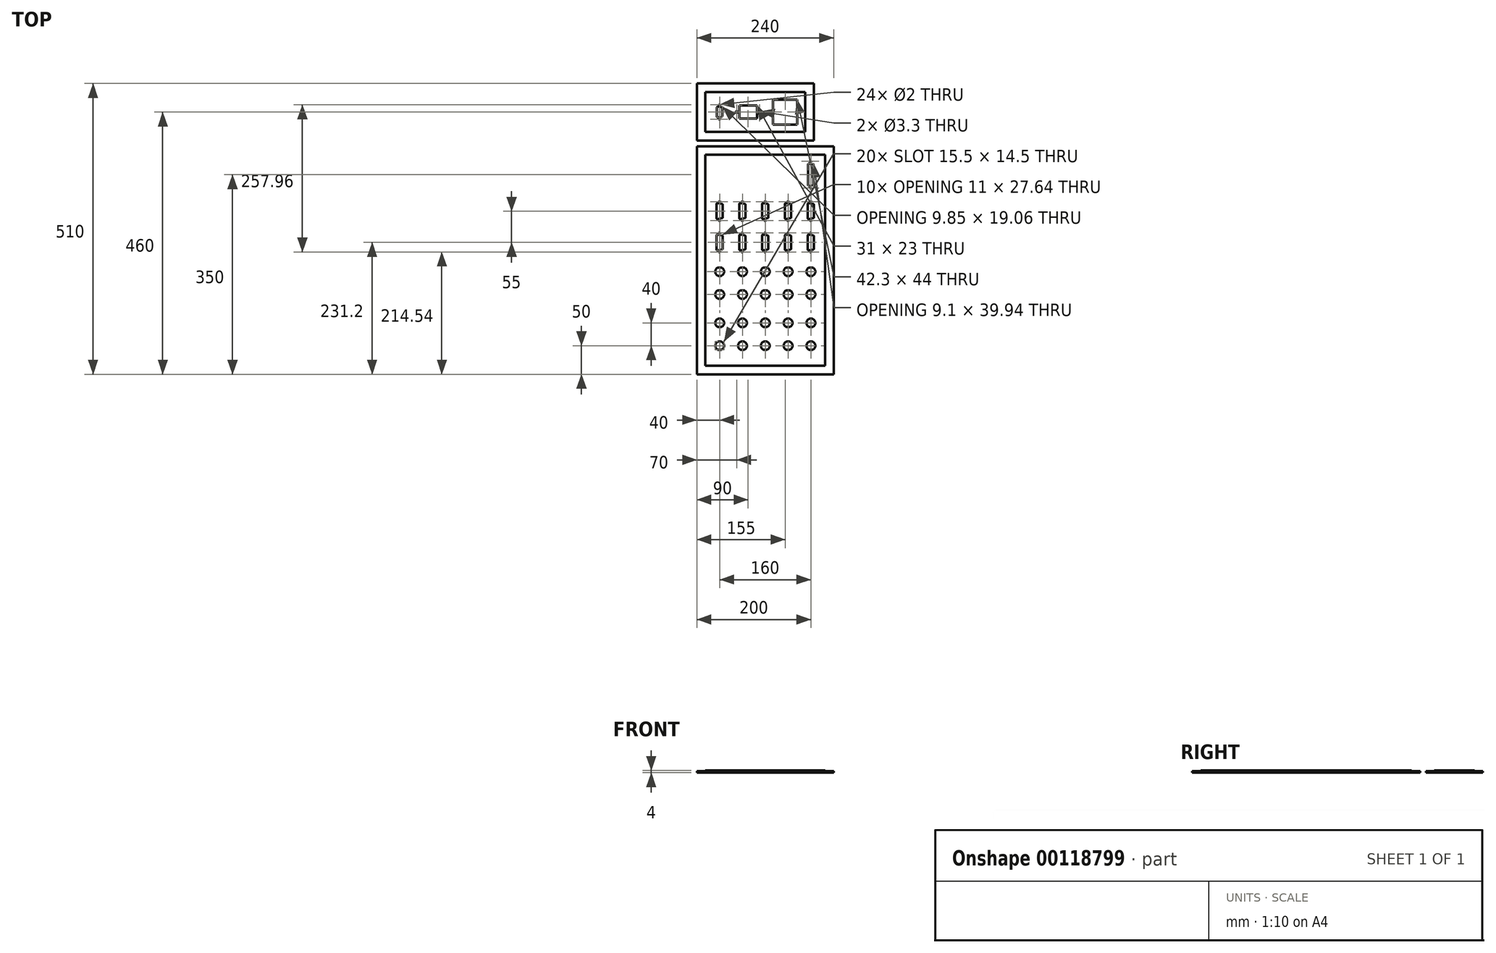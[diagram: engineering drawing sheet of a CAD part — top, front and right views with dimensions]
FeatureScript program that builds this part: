
annotation { "Feature Type Name" : "Feature", "Feature Type Description" : "" }
export const myFeature = defineFeature(function(context is Context, id is Id, definition is map)
    precondition{}
    {
        {
            var Q0;
            Q0=qCreatedBy(makeId("Top.planeOp"),FACE);
            var sketch = newSketch(context, id + "F0", { "sketchPlane" : qUnion([Q0])});
            skLineSegment(sketch, "E0.bottom", {"start": v(-120, -200) * mm, "end": v(120, -200) * mm});
            skLineSegment(sketch, "E0.top", {"start": v(-120, 200) * mm, "end": v(120, 200) * mm});
            skLineSegment(sketch, "E0.left", {"start": v(-120, -200) * mm, "end": v(-120, 200) * mm});
            skLineSegment(sketch, "E0.right", {"start": v(120, -200) * mm, "end": v(120, 200) * mm});
            skArc(sketch, "E1", {"start": v(-82.74, -102.75) * mm, "mid": v(-87.75, -110) * mm, "end": v(-82.74, -117.25) * mm});
            skLineSegment(sketch, "E2", {"start": v(-82.74, -102.75) * mm, "end": v(-77.26, -102.75) * mm});
            skLineSegment(sketch, "E3", {"start": v(-77.26, -117.25) * mm, "end": v(-82.74, -117.25) * mm});
            skLineSegment(sketch, "E4", {"start": v(-80, -110) * mm, "end": v(-87.75, -110) * mm, "construction": true});
            skArc(sketch, "E5.trimOffspring", {"start": v(-77.26, -117.25) * mm, "mid": v(-72.25, -110) * mm, "end": v(-77.26, -102.75) * mm});
            skLineSegment(sketch, "E6.0.1.0", {"start": v(-77.26, -157.25) * mm, "end": v(-82.74, -157.25) * mm});
            skLineSegment(sketch, "E6.0.1.1", {"start": v(-82.74, -142.75) * mm, "end": v(-77.26, -142.75) * mm});
            skArc(sketch, "E6.0.1.2", {"start": v(-82.74, -142.75) * mm, "mid": v(-87.75, -150) * mm, "end": v(-82.74, -157.25) * mm});
            skLineSegment(sketch, "E6.0.1.3", {"start": v(-80, -150) * mm, "end": v(-87.75, -150) * mm, "construction": true});
            skArc(sketch, "E6.0.1.4", {"start": v(-77.26, -157.25) * mm, "mid": v(-72.25, -150) * mm, "end": v(-77.26, -142.75) * mm});
            skLineSegment(sketch, "E6.direction1", {"start": v(-82.74, -117.25) * mm, "end": v(-42.74, -117.25) * mm, "construction": true});
            skLineSegment(sketch, "E6.direction2", {"start": v(-82.74, -117.25) * mm, "end": v(-82.74, -157.25) * mm, "construction": true});
            skLineSegment(sketch, "E7.0.1.0", {"start": v(-37.26, -117.25) * mm, "end": v(-42.74, -117.25) * mm});
            skLineSegment(sketch, "E7.3.1.0", {"start": v(-42.74, -102.75) * mm, "end": v(-37.26, -102.75) * mm});
            skArc(sketch, "E7.6.1.0", {"start": v(-42.74, -102.75) * mm, "mid": v(-47.75, -110) * mm, "end": v(-42.74, -117.25) * mm});
            skLineSegment(sketch, "E7.10.1.0", {"start": v(-40, -110) * mm, "end": v(-47.75, -110) * mm, "construction": true});
            skArc(sketch, "E7.13.1.0", {"start": v(-37.26, -117.25) * mm, "mid": v(-32.25, -110) * mm, "end": v(-37.26, -102.75) * mm});
            skLineSegment(sketch, "E7.0.1.1", {"start": v(-37.26, -157.25) * mm, "end": v(-42.74, -157.25) * mm});
            skLineSegment(sketch, "E7.3.1.1", {"start": v(-42.74, -142.75) * mm, "end": v(-37.26, -142.75) * mm});
            skArc(sketch, "E7.6.1.1", {"start": v(-42.74, -142.75) * mm, "mid": v(-47.75, -150) * mm, "end": v(-42.74, -157.25) * mm});
            skLineSegment(sketch, "E7.10.1.1", {"start": v(-40, -150) * mm, "end": v(-47.75, -150) * mm, "construction": true});
            skArc(sketch, "E7.13.1.1", {"start": v(-37.26, -157.25) * mm, "mid": v(-32.25, -150) * mm, "end": v(-37.26, -142.75) * mm});
            skLineSegment(sketch, "E7.0.2.0", {"start": v(2.74, -117.25) * mm, "end": v(-2.74, -117.25) * mm});
            skLineSegment(sketch, "E7.3.2.0", {"start": v(-2.74, -102.75) * mm, "end": v(2.74, -102.75) * mm});
            skArc(sketch, "E7.6.2.0", {"start": v(-2.74, -102.75) * mm, "mid": v(-7.75, -110) * mm, "end": v(-2.74, -117.25) * mm});
            skLineSegment(sketch, "E7.10.2.0", {"start": v(0, -110) * mm, "end": v(-7.75, -110) * mm, "construction": true});
            skArc(sketch, "E7.13.2.0", {"start": v(2.74, -117.25) * mm, "mid": v(7.75, -110) * mm, "end": v(2.74, -102.75) * mm});
            skLineSegment(sketch, "E7.0.2.1", {"start": v(2.74, -157.25) * mm, "end": v(-2.74, -157.25) * mm});
            skLineSegment(sketch, "E7.3.2.1", {"start": v(-2.74, -142.75) * mm, "end": v(2.74, -142.75) * mm});
            skArc(sketch, "E7.6.2.1", {"start": v(-2.74, -142.75) * mm, "mid": v(-7.75, -150) * mm, "end": v(-2.74, -157.25) * mm});
            skLineSegment(sketch, "E7.10.2.1", {"start": v(0, -150) * mm, "end": v(-7.75, -150) * mm, "construction": true});
            skArc(sketch, "E7.13.2.1", {"start": v(2.74, -157.25) * mm, "mid": v(7.75, -150) * mm, "end": v(2.74, -142.75) * mm});
            skLineSegment(sketch, "E7.0.3.0", {"start": v(42.74, -117.25) * mm, "end": v(37.26, -117.25) * mm});
            skLineSegment(sketch, "E7.3.3.0", {"start": v(37.26, -102.75) * mm, "end": v(42.74, -102.75) * mm});
            skArc(sketch, "E7.6.3.0", {"start": v(37.26, -102.75) * mm, "mid": v(32.25, -110) * mm, "end": v(37.26, -117.25) * mm});
            skLineSegment(sketch, "E7.10.3.0", {"start": v(40, -110) * mm, "end": v(32.25, -110) * mm, "construction": true});
            skArc(sketch, "E7.13.3.0", {"start": v(42.74, -117.25) * mm, "mid": v(47.75, -110) * mm, "end": v(42.74, -102.75) * mm});
            skLineSegment(sketch, "E7.0.3.1", {"start": v(42.74, -157.25) * mm, "end": v(37.26, -157.25) * mm});
            skLineSegment(sketch, "E7.3.3.1", {"start": v(37.26, -142.75) * mm, "end": v(42.74, -142.75) * mm});
            skArc(sketch, "E7.6.3.1", {"start": v(37.26, -142.75) * mm, "mid": v(32.25, -150) * mm, "end": v(37.26, -157.25) * mm});
            skLineSegment(sketch, "E7.10.3.1", {"start": v(40, -150) * mm, "end": v(32.25, -150) * mm, "construction": true});
            skArc(sketch, "E7.13.3.1", {"start": v(42.74, -157.25) * mm, "mid": v(47.75, -150) * mm, "end": v(42.74, -142.75) * mm});
            skLineSegment(sketch, "E7.0.4.0", {"start": v(82.74, -117.25) * mm, "end": v(77.26, -117.25) * mm});
            skLineSegment(sketch, "E7.3.4.0", {"start": v(77.26, -102.75) * mm, "end": v(82.74, -102.75) * mm});
            skArc(sketch, "E7.6.4.0", {"start": v(77.26, -102.75) * mm, "mid": v(72.25, -110) * mm, "end": v(77.26, -117.25) * mm});
            skLineSegment(sketch, "E7.10.4.0", {"start": v(80, -110) * mm, "end": v(72.25, -110) * mm, "construction": true});
            skArc(sketch, "E7.13.4.0", {"start": v(82.74, -117.25) * mm, "mid": v(87.75, -110) * mm, "end": v(82.74, -102.75) * mm});
            skLineSegment(sketch, "E7.0.4.1", {"start": v(82.74, -157.25) * mm, "end": v(77.26, -157.25) * mm});
            skLineSegment(sketch, "E7.3.4.1", {"start": v(77.26, -142.75) * mm, "end": v(82.74, -142.75) * mm});
            skArc(sketch, "E7.6.4.1", {"start": v(77.26, -142.75) * mm, "mid": v(72.25, -150) * mm, "end": v(77.26, -157.25) * mm});
            skLineSegment(sketch, "E7.10.4.1", {"start": v(80, -150) * mm, "end": v(72.25, -150) * mm, "construction": true});
            skArc(sketch, "E7.13.4.1", {"start": v(82.74, -157.25) * mm, "mid": v(87.75, -150) * mm, "end": v(82.74, -142.75) * mm});
            skLineSegment(sketch, "E8.bottom", {"start": v(-105, 185) * mm, "end": v(105, 185) * mm, "construction": true});
            skLineSegment(sketch, "E8.top", {"start": v(-105, -185) * mm, "end": v(105, -185) * mm, "construction": true});
            skLineSegment(sketch, "E8.left", {"start": v(-105, 185) * mm, "end": v(-105, -185) * mm, "construction": true});
            skLineSegment(sketch, "E8.right", {"start": v(105, 185) * mm, "end": v(105, -185) * mm, "construction": true});
            skArc(sketch, "E9", {"start": v(-82.74, -12.75) * mm, "mid": v(-87.75, -20) * mm, "end": v(-82.74, -27.25) * mm});
            skLineSegment(sketch, "E10", {"start": v(-82.74, -12.75) * mm, "end": v(-77.26, -12.75) * mm});
            skLineSegment(sketch, "E11", {"start": v(-77.26, -27.25) * mm, "end": v(-82.74, -27.25) * mm});
            skLineSegment(sketch, "E12", {"start": v(-80, -20) * mm, "end": v(-87.75, -20) * mm, "construction": true});
            skArc(sketch, "E13.trimOffspring", {"start": v(-77.26, -27.25) * mm, "mid": v(-72.25, -20) * mm, "end": v(-77.26, -12.75) * mm});
            skLineSegment(sketch, "E14", {"start": v(-83.74, 100) * mm, "end": v(-75.74, 98.59) * mm});
            skLineSegment(sketch, "E15", {"start": v(-74.5, 97.11) * mm, "end": v(-74.5, 75.29) * mm});
            skLineSegment(sketch, "E16", {"start": v(-75.74, 73.81) * mm, "end": v(-83.74, 72.4) * mm});
            skLineSegment(sketch, "E17", {"start": v(-85.5, 73.88) * mm, "end": v(-85.5, 98.52) * mm});
            skLineSegment(sketch, "E18", {"start": v(-80, 99.34) * mm, "end": v(-80, 73.06) * mm, "construction": true});
            skPoint(sketch, "E19.visualSharp", {"position": v(-85.5, 100.31) * mm});
            skArc(sketch, "E19.filletArc", {"start": v(-83.74, 100) * mm, "mid": v(-84.96, 99.67) * mm, "end": v(-85.5, 98.52) * mm});
            skPoint(sketch, "E20.visualSharp", {"position": v(-74.5, 98.37) * mm});
            skArc(sketch, "E20.filletArc", {"start": v(-74.5, 97.11) * mm, "mid": v(-74.85, 98.08) * mm, "end": v(-75.74, 98.59) * mm});
            skPoint(sketch, "E21.visualSharp", {"position": v(-74.5, 74.03) * mm});
            skArc(sketch, "E21.filletArc", {"start": v(-75.74, 73.81) * mm, "mid": v(-74.85, 74.32) * mm, "end": v(-74.5, 75.29) * mm});
            skPoint(sketch, "E22.visualSharp", {"position": v(-85.5, 72.09) * mm});
            skArc(sketch, "E22.filletArc", {"start": v(-85.5, 73.88) * mm, "mid": v(-84.96, 72.73) * mm, "end": v(-83.74, 72.4) * mm});
            skCircle(sketch, "E23", {"center": v(-80, 102.86) * mm, "radius": 1 * mm});
            skCircle(sketch, "E24", {"center": v(-80, 69.54) * mm, "radius": 1 * mm});
            skLineSegment(sketch, "E25", {"start": v(-84, 86.2) * mm, "end": v(-76.01, 86.2) * mm, "construction": true});
            skPoint(sketch, "E26.0.1.0", {"position": v(-85.5, 45.31) * mm});
            skPoint(sketch, "E26.0.1.1", {"position": v(-85.5, 17.09) * mm});
            skPoint(sketch, "E26.0.1.2", {"position": v(-74.5, 43.37) * mm});
            skLineSegment(sketch, "E26.0.1.3", {"start": v(-80, 44.34) * mm, "end": v(-80, 18.06) * mm, "construction": true});
            skLineSegment(sketch, "E26.0.1.4", {"start": v(-84, 31.2) * mm, "end": v(-76.01, 31.2) * mm, "construction": true});
            skPoint(sketch, "E26.0.1.5", {"position": v(-74.5, 19.03) * mm});
            skLineSegment(sketch, "E26.0.1.6", {"start": v(-74.5, 42.11) * mm, "end": v(-74.5, 20.29) * mm});
            skLineSegment(sketch, "E26.0.1.7", {"start": v(-85.5, 18.88) * mm, "end": v(-85.5, 43.52) * mm});
            skCircle(sketch, "E26.0.1.8", {"center": v(-80, 47.86) * mm, "radius": 1 * mm});
            skLineSegment(sketch, "E26.0.1.9", {"start": v(-83.74, 45) * mm, "end": v(-75.74, 43.59) * mm});
            skCircle(sketch, "E26.0.1.10", {"center": v(-80, 14.54) * mm, "radius": 1 * mm});
            skArc(sketch, "E26.0.1.11", {"start": v(-83.74, 45) * mm, "mid": v(-84.96, 44.67) * mm, "end": v(-85.5, 43.52) * mm});
            skArc(sketch, "E26.0.1.12", {"start": v(-85.5, 18.88) * mm, "mid": v(-84.96, 17.73) * mm, "end": v(-83.74, 17.4) * mm});
            skLineSegment(sketch, "E26.0.1.13", {"start": v(-75.74, 18.81) * mm, "end": v(-83.74, 17.4) * mm});
            skArc(sketch, "E26.0.1.14", {"start": v(-75.74, 18.81) * mm, "mid": v(-74.85, 19.32) * mm, "end": v(-74.5, 20.29) * mm});
            skArc(sketch, "E26.0.1.15", {"start": v(-74.5, 42.11) * mm, "mid": v(-74.85, 43.08) * mm, "end": v(-75.74, 43.59) * mm});
            skPoint(sketch, "E26.1.0.0", {"position": v(-45.5, 100.31) * mm});
            skPoint(sketch, "E26.1.0.1", {"position": v(-45.5, 72.09) * mm});
            skPoint(sketch, "E26.1.0.2", {"position": v(-34.5, 98.37) * mm});
            skLineSegment(sketch, "E26.1.0.3", {"start": v(-40, 99.34) * mm, "end": v(-40, 73.06) * mm, "construction": true});
            skLineSegment(sketch, "E26.1.0.4", {"start": v(-44, 86.2) * mm, "end": v(-36.01, 86.2) * mm, "construction": true});
            skPoint(sketch, "E26.1.0.5", {"position": v(-34.5, 74.03) * mm});
            skLineSegment(sketch, "E26.1.0.6", {"start": v(-34.5, 97.11) * mm, "end": v(-34.5, 75.29) * mm});
            skLineSegment(sketch, "E26.1.0.7", {"start": v(-45.5, 73.88) * mm, "end": v(-45.5, 98.52) * mm});
            skCircle(sketch, "E26.1.0.8", {"center": v(-40, 102.86) * mm, "radius": 1 * mm});
            skLineSegment(sketch, "E26.1.0.9", {"start": v(-43.74, 100) * mm, "end": v(-35.74, 98.59) * mm});
            skCircle(sketch, "E26.1.0.10", {"center": v(-40, 69.54) * mm, "radius": 1 * mm});
            skArc(sketch, "E26.1.0.11", {"start": v(-43.74, 100) * mm, "mid": v(-44.96, 99.67) * mm, "end": v(-45.5, 98.52) * mm});
            skArc(sketch, "E26.1.0.12", {"start": v(-45.5, 73.88) * mm, "mid": v(-44.96, 72.73) * mm, "end": v(-43.74, 72.4) * mm});
            skLineSegment(sketch, "E26.1.0.13", {"start": v(-35.74, 73.81) * mm, "end": v(-43.74, 72.4) * mm});
            skArc(sketch, "E26.1.0.14", {"start": v(-35.74, 73.81) * mm, "mid": v(-34.85, 74.32) * mm, "end": v(-34.5, 75.29) * mm});
            skArc(sketch, "E26.1.0.15", {"start": v(-34.5, 97.11) * mm, "mid": v(-34.85, 98.08) * mm, "end": v(-35.74, 98.59) * mm});
            skPoint(sketch, "E26.1.1.0", {"position": v(-45.5, 45.31) * mm});
            skPoint(sketch, "E26.1.1.1", {"position": v(-45.5, 17.09) * mm});
            skPoint(sketch, "E26.1.1.2", {"position": v(-34.5, 43.37) * mm});
            skLineSegment(sketch, "E26.1.1.3", {"start": v(-40, 44.34) * mm, "end": v(-40, 18.06) * mm, "construction": true});
            skLineSegment(sketch, "E26.1.1.4", {"start": v(-44, 31.2) * mm, "end": v(-36.01, 31.2) * mm, "construction": true});
            skPoint(sketch, "E26.1.1.5", {"position": v(-34.5, 19.03) * mm});
            skLineSegment(sketch, "E26.1.1.6", {"start": v(-34.5, 42.11) * mm, "end": v(-34.5, 20.29) * mm});
            skLineSegment(sketch, "E26.1.1.7", {"start": v(-45.5, 18.88) * mm, "end": v(-45.5, 43.52) * mm});
            skCircle(sketch, "E26.1.1.8", {"center": v(-40, 47.86) * mm, "radius": 1 * mm});
            skLineSegment(sketch, "E26.1.1.9", {"start": v(-43.74, 45) * mm, "end": v(-35.74, 43.59) * mm});
            skCircle(sketch, "E26.1.1.10", {"center": v(-40, 14.54) * mm, "radius": 1 * mm});
            skArc(sketch, "E26.1.1.11", {"start": v(-43.74, 45) * mm, "mid": v(-44.96, 44.67) * mm, "end": v(-45.5, 43.52) * mm});
            skArc(sketch, "E26.1.1.12", {"start": v(-45.5, 18.88) * mm, "mid": v(-44.96, 17.73) * mm, "end": v(-43.74, 17.4) * mm});
            skLineSegment(sketch, "E26.1.1.13", {"start": v(-35.74, 18.81) * mm, "end": v(-43.74, 17.4) * mm});
            skArc(sketch, "E26.1.1.14", {"start": v(-35.74, 18.81) * mm, "mid": v(-34.85, 19.32) * mm, "end": v(-34.5, 20.29) * mm});
            skArc(sketch, "E26.1.1.15", {"start": v(-34.5, 42.11) * mm, "mid": v(-34.85, 43.08) * mm, "end": v(-35.74, 43.59) * mm});
            skPoint(sketch, "E26.2.0.0", {"position": v(-5.5, 100.31) * mm});
            skPoint(sketch, "E26.2.0.1", {"position": v(-5.5, 72.09) * mm});
            skPoint(sketch, "E26.2.0.2", {"position": v(5.5, 98.37) * mm});
            skLineSegment(sketch, "E26.2.0.3", {"start": v(0, 99.34) * mm, "end": v(0, 73.06) * mm, "construction": true});
            skLineSegment(sketch, "E26.2.0.4", {"start": v(-4, 86.2) * mm, "end": v(3.99, 86.2) * mm, "construction": true});
            skPoint(sketch, "E26.2.0.5", {"position": v(5.5, 74.03) * mm});
            skLineSegment(sketch, "E26.2.0.6", {"start": v(5.5, 97.11) * mm, "end": v(5.5, 75.29) * mm});
            skLineSegment(sketch, "E26.2.0.7", {"start": v(-5.5, 73.88) * mm, "end": v(-5.5, 98.52) * mm});
            skCircle(sketch, "E26.2.0.8", {"center": v(0, 102.86) * mm, "radius": 1 * mm});
            skLineSegment(sketch, "E26.2.0.9", {"start": v(-3.74, 100) * mm, "end": v(4.26, 98.59) * mm});
            skCircle(sketch, "E26.2.0.10", {"center": v(0, 69.54) * mm, "radius": 1 * mm});
            skArc(sketch, "E26.2.0.11", {"start": v(-3.74, 100) * mm, "mid": v(-4.96, 99.67) * mm, "end": v(-5.5, 98.52) * mm});
            skArc(sketch, "E26.2.0.12", {"start": v(-5.5, 73.88) * mm, "mid": v(-4.96, 72.73) * mm, "end": v(-3.74, 72.4) * mm});
            skLineSegment(sketch, "E26.2.0.13", {"start": v(4.26, 73.81) * mm, "end": v(-3.74, 72.4) * mm});
            skArc(sketch, "E26.2.0.14", {"start": v(4.26, 73.81) * mm, "mid": v(5.15, 74.32) * mm, "end": v(5.5, 75.29) * mm});
            skArc(sketch, "E26.2.0.15", {"start": v(5.5, 97.11) * mm, "mid": v(5.15, 98.08) * mm, "end": v(4.26, 98.59) * mm});
            skPoint(sketch, "E26.2.1.0", {"position": v(-5.5, 45.31) * mm});
            skPoint(sketch, "E26.2.1.1", {"position": v(-5.5, 17.09) * mm});
            skPoint(sketch, "E26.2.1.2", {"position": v(5.5, 43.37) * mm});
            skLineSegment(sketch, "E26.2.1.3", {"start": v(0, 44.34) * mm, "end": v(0, 18.06) * mm, "construction": true});
            skLineSegment(sketch, "E26.2.1.4", {"start": v(-4, 31.2) * mm, "end": v(3.99, 31.2) * mm, "construction": true});
            skPoint(sketch, "E26.2.1.5", {"position": v(5.5, 19.03) * mm});
            skLineSegment(sketch, "E26.2.1.6", {"start": v(5.5, 42.11) * mm, "end": v(5.5, 20.29) * mm});
            skLineSegment(sketch, "E26.2.1.7", {"start": v(-5.5, 18.88) * mm, "end": v(-5.5, 43.52) * mm});
            skCircle(sketch, "E26.2.1.8", {"center": v(0, 47.86) * mm, "radius": 1 * mm});
            skLineSegment(sketch, "E26.2.1.9", {"start": v(-3.74, 45) * mm, "end": v(4.26, 43.59) * mm});
            skCircle(sketch, "E26.2.1.10", {"center": v(0, 14.54) * mm, "radius": 1 * mm});
            skArc(sketch, "E26.2.1.11", {"start": v(-3.74, 45) * mm, "mid": v(-4.96, 44.67) * mm, "end": v(-5.5, 43.52) * mm});
            skArc(sketch, "E26.2.1.12", {"start": v(-5.5, 18.88) * mm, "mid": v(-4.96, 17.73) * mm, "end": v(-3.74, 17.4) * mm});
            skLineSegment(sketch, "E26.2.1.13", {"start": v(4.26, 18.81) * mm, "end": v(-3.74, 17.4) * mm});
            skArc(sketch, "E26.2.1.14", {"start": v(4.26, 18.81) * mm, "mid": v(5.15, 19.32) * mm, "end": v(5.5, 20.29) * mm});
            skArc(sketch, "E26.2.1.15", {"start": v(5.5, 42.11) * mm, "mid": v(5.15, 43.08) * mm, "end": v(4.26, 43.59) * mm});
            skPoint(sketch, "E26.3.0.0", {"position": v(34.5, 100.31) * mm});
            skPoint(sketch, "E26.3.0.1", {"position": v(34.5, 72.09) * mm});
            skPoint(sketch, "E26.3.0.2", {"position": v(45.5, 98.37) * mm});
            skLineSegment(sketch, "E26.3.0.3", {"start": v(40, 99.34) * mm, "end": v(40, 73.06) * mm, "construction": true});
            skLineSegment(sketch, "E26.3.0.4", {"start": v(36, 86.2) * mm, "end": v(43.99, 86.2) * mm, "construction": true});
            skPoint(sketch, "E26.3.0.5", {"position": v(45.5, 74.03) * mm});
            skLineSegment(sketch, "E26.3.0.6", {"start": v(45.5, 97.11) * mm, "end": v(45.5, 75.29) * mm});
            skLineSegment(sketch, "E26.3.0.7", {"start": v(34.5, 73.88) * mm, "end": v(34.5, 98.52) * mm});
            skCircle(sketch, "E26.3.0.8", {"center": v(40, 102.86) * mm, "radius": 1 * mm});
            skLineSegment(sketch, "E26.3.0.9", {"start": v(36.26, 100) * mm, "end": v(44.26, 98.59) * mm});
            skCircle(sketch, "E26.3.0.10", {"center": v(40, 69.54) * mm, "radius": 1 * mm});
            skArc(sketch, "E26.3.0.11", {"start": v(36.26, 100) * mm, "mid": v(35.04, 99.67) * mm, "end": v(34.5, 98.52) * mm});
            skArc(sketch, "E26.3.0.12", {"start": v(34.5, 73.88) * mm, "mid": v(35.04, 72.73) * mm, "end": v(36.26, 72.4) * mm});
            skLineSegment(sketch, "E26.3.0.13", {"start": v(44.26, 73.81) * mm, "end": v(36.26, 72.4) * mm});
            skArc(sketch, "E26.3.0.14", {"start": v(44.26, 73.81) * mm, "mid": v(45.15, 74.32) * mm, "end": v(45.5, 75.29) * mm});
            skArc(sketch, "E26.3.0.15", {"start": v(45.5, 97.11) * mm, "mid": v(45.15, 98.08) * mm, "end": v(44.26, 98.59) * mm});
            skPoint(sketch, "E26.3.1.0", {"position": v(34.5, 45.31) * mm});
            skPoint(sketch, "E26.3.1.1", {"position": v(34.5, 17.09) * mm});
            skPoint(sketch, "E26.3.1.2", {"position": v(45.5, 43.37) * mm});
            skLineSegment(sketch, "E26.3.1.3", {"start": v(40, 44.34) * mm, "end": v(40, 18.06) * mm, "construction": true});
            skLineSegment(sketch, "E26.3.1.4", {"start": v(36, 31.2) * mm, "end": v(43.99, 31.2) * mm, "construction": true});
            skPoint(sketch, "E26.3.1.5", {"position": v(45.5, 19.03) * mm});
            skLineSegment(sketch, "E26.3.1.6", {"start": v(45.5, 42.11) * mm, "end": v(45.5, 20.29) * mm});
            skLineSegment(sketch, "E26.3.1.7", {"start": v(34.5, 18.88) * mm, "end": v(34.5, 43.52) * mm});
            skCircle(sketch, "E26.3.1.8", {"center": v(40, 47.86) * mm, "radius": 1 * mm});
            skLineSegment(sketch, "E26.3.1.9", {"start": v(36.26, 45) * mm, "end": v(44.26, 43.59) * mm});
            skCircle(sketch, "E26.3.1.10", {"center": v(40, 14.54) * mm, "radius": 1 * mm});
            skArc(sketch, "E26.3.1.11", {"start": v(36.26, 45) * mm, "mid": v(35.04, 44.67) * mm, "end": v(34.5, 43.52) * mm});
            skArc(sketch, "E26.3.1.12", {"start": v(34.5, 18.88) * mm, "mid": v(35.04, 17.73) * mm, "end": v(36.26, 17.4) * mm});
            skLineSegment(sketch, "E26.3.1.13", {"start": v(44.26, 18.81) * mm, "end": v(36.26, 17.4) * mm});
            skArc(sketch, "E26.3.1.14", {"start": v(44.26, 18.81) * mm, "mid": v(45.15, 19.32) * mm, "end": v(45.5, 20.29) * mm});
            skArc(sketch, "E26.3.1.15", {"start": v(45.5, 42.11) * mm, "mid": v(45.15, 43.08) * mm, "end": v(44.26, 43.59) * mm});
            skPoint(sketch, "E26.4.0.0", {"position": v(74.5, 100.31) * mm});
            skPoint(sketch, "E26.4.0.1", {"position": v(74.5, 72.09) * mm});
            skPoint(sketch, "E26.4.0.2", {"position": v(85.5, 98.37) * mm});
            skLineSegment(sketch, "E26.4.0.3", {"start": v(80, 99.34) * mm, "end": v(80, 73.06) * mm, "construction": true});
            skLineSegment(sketch, "E26.4.0.4", {"start": v(76, 86.2) * mm, "end": v(83.99, 86.2) * mm, "construction": true});
            skPoint(sketch, "E26.4.0.5", {"position": v(85.5, 74.03) * mm});
            skLineSegment(sketch, "E26.4.0.6", {"start": v(85.5, 97.11) * mm, "end": v(85.5, 75.29) * mm});
            skLineSegment(sketch, "E26.4.0.7", {"start": v(74.5, 73.88) * mm, "end": v(74.5, 98.52) * mm});
            skCircle(sketch, "E26.4.0.8", {"center": v(80, 102.86) * mm, "radius": 1 * mm});
            skLineSegment(sketch, "E26.4.0.9", {"start": v(76.26, 100) * mm, "end": v(84.26, 98.59) * mm});
            skCircle(sketch, "E26.4.0.10", {"center": v(80, 69.54) * mm, "radius": 1 * mm});
            skArc(sketch, "E26.4.0.11", {"start": v(76.26, 100) * mm, "mid": v(75.04, 99.67) * mm, "end": v(74.5, 98.52) * mm});
            skArc(sketch, "E26.4.0.12", {"start": v(74.5, 73.88) * mm, "mid": v(75.04, 72.73) * mm, "end": v(76.26, 72.4) * mm});
            skLineSegment(sketch, "E26.4.0.13", {"start": v(84.26, 73.81) * mm, "end": v(76.26, 72.4) * mm});
            skArc(sketch, "E26.4.0.14", {"start": v(84.26, 73.81) * mm, "mid": v(85.15, 74.32) * mm, "end": v(85.5, 75.29) * mm});
            skArc(sketch, "E26.4.0.15", {"start": v(85.5, 97.11) * mm, "mid": v(85.15, 98.08) * mm, "end": v(84.26, 98.59) * mm});
            skPoint(sketch, "E26.4.1.0", {"position": v(74.5, 45.31) * mm});
            skPoint(sketch, "E26.4.1.1", {"position": v(74.5, 17.09) * mm});
            skPoint(sketch, "E26.4.1.2", {"position": v(85.5, 43.37) * mm});
            skLineSegment(sketch, "E26.4.1.3", {"start": v(80, 44.34) * mm, "end": v(80, 18.06) * mm, "construction": true});
            skLineSegment(sketch, "E26.4.1.4", {"start": v(76, 31.2) * mm, "end": v(83.99, 31.2) * mm, "construction": true});
            skPoint(sketch, "E26.4.1.5", {"position": v(85.5, 19.03) * mm});
            skLineSegment(sketch, "E26.4.1.6", {"start": v(85.5, 42.11) * mm, "end": v(85.5, 20.29) * mm});
            skLineSegment(sketch, "E26.4.1.7", {"start": v(74.5, 18.88) * mm, "end": v(74.5, 43.52) * mm});
            skCircle(sketch, "E26.4.1.8", {"center": v(80, 47.86) * mm, "radius": 1 * mm});
            skLineSegment(sketch, "E26.4.1.9", {"start": v(76.26, 45) * mm, "end": v(84.26, 43.59) * mm});
            skCircle(sketch, "E26.4.1.10", {"center": v(80, 14.54) * mm, "radius": 1 * mm});
            skArc(sketch, "E26.4.1.11", {"start": v(76.26, 45) * mm, "mid": v(75.04, 44.67) * mm, "end": v(74.5, 43.52) * mm});
            skArc(sketch, "E26.4.1.12", {"start": v(74.5, 18.88) * mm, "mid": v(75.04, 17.73) * mm, "end": v(76.26, 17.4) * mm});
            skLineSegment(sketch, "E26.4.1.13", {"start": v(84.26, 18.81) * mm, "end": v(76.26, 17.4) * mm});
            skArc(sketch, "E26.4.1.14", {"start": v(84.26, 18.81) * mm, "mid": v(85.15, 19.32) * mm, "end": v(85.5, 20.29) * mm});
            skArc(sketch, "E26.4.1.15", {"start": v(85.5, 42.11) * mm, "mid": v(85.15, 43.08) * mm, "end": v(84.26, 43.59) * mm});
            skLineSegment(sketch, "E26.direction1", {"start": v(-85.5, 72.09) * mm, "end": v(-45.5, 72.09) * mm, "construction": true});
            skLineSegment(sketch, "E26.direction2", {"start": v(-85.5, 72.09) * mm, "end": v(-85.5, 17.09) * mm, "construction": true});
            skLineSegment(sketch, "E27.0.1.0", {"start": v(-80, -60) * mm, "end": v(-87.75, -60) * mm, "construction": true});
            skArc(sketch, "E27.0.1.1", {"start": v(-77.26, -67.25) * mm, "mid": v(-72.25, -60) * mm, "end": v(-77.26, -52.75) * mm});
            skArc(sketch, "E27.0.1.2", {"start": v(-82.74, -52.75) * mm, "mid": v(-87.75, -60) * mm, "end": v(-82.74, -67.25) * mm});
            skLineSegment(sketch, "E27.0.1.3", {"start": v(-82.74, -52.75) * mm, "end": v(-77.26, -52.75) * mm});
            skLineSegment(sketch, "E27.0.1.4", {"start": v(-77.26, -67.25) * mm, "end": v(-82.74, -67.25) * mm});
            skLineSegment(sketch, "E27.1.0.0", {"start": v(-40, -20) * mm, "end": v(-47.75, -20) * mm, "construction": true});
            skArc(sketch, "E27.1.0.1", {"start": v(-37.26, -27.25) * mm, "mid": v(-32.25, -20) * mm, "end": v(-37.26, -12.75) * mm});
            skArc(sketch, "E27.1.0.2", {"start": v(-42.74, -12.75) * mm, "mid": v(-47.75, -20) * mm, "end": v(-42.74, -27.25) * mm});
            skLineSegment(sketch, "E27.1.0.3", {"start": v(-42.74, -12.75) * mm, "end": v(-37.26, -12.75) * mm});
            skLineSegment(sketch, "E27.1.0.4", {"start": v(-37.26, -27.25) * mm, "end": v(-42.74, -27.25) * mm});
            skLineSegment(sketch, "E27.1.1.0", {"start": v(-40, -60) * mm, "end": v(-47.75, -60) * mm, "construction": true});
            skArc(sketch, "E27.1.1.1", {"start": v(-37.26, -67.25) * mm, "mid": v(-32.25, -60) * mm, "end": v(-37.26, -52.75) * mm});
            skArc(sketch, "E27.1.1.2", {"start": v(-42.74, -52.75) * mm, "mid": v(-47.75, -60) * mm, "end": v(-42.74, -67.25) * mm});
            skLineSegment(sketch, "E27.1.1.3", {"start": v(-42.74, -52.75) * mm, "end": v(-37.26, -52.75) * mm});
            skLineSegment(sketch, "E27.1.1.4", {"start": v(-37.26, -67.25) * mm, "end": v(-42.74, -67.25) * mm});
            skLineSegment(sketch, "E27.2.0.0", {"start": v(0, -20) * mm, "end": v(-7.75, -20) * mm, "construction": true});
            skArc(sketch, "E27.2.0.1", {"start": v(2.74, -27.25) * mm, "mid": v(7.75, -20) * mm, "end": v(2.74, -12.75) * mm});
            skArc(sketch, "E27.2.0.2", {"start": v(-2.74, -12.75) * mm, "mid": v(-7.75, -20) * mm, "end": v(-2.74, -27.25) * mm});
            skLineSegment(sketch, "E27.2.0.3", {"start": v(-2.74, -12.75) * mm, "end": v(2.74, -12.75) * mm});
            skLineSegment(sketch, "E27.2.0.4", {"start": v(2.74, -27.25) * mm, "end": v(-2.74, -27.25) * mm});
            skLineSegment(sketch, "E27.2.1.0", {"start": v(0, -60) * mm, "end": v(-7.75, -60) * mm, "construction": true});
            skArc(sketch, "E27.2.1.1", {"start": v(2.74, -67.25) * mm, "mid": v(7.75, -60) * mm, "end": v(2.74, -52.75) * mm});
            skArc(sketch, "E27.2.1.2", {"start": v(-2.74, -52.75) * mm, "mid": v(-7.75, -60) * mm, "end": v(-2.74, -67.25) * mm});
            skLineSegment(sketch, "E27.2.1.3", {"start": v(-2.74, -52.75) * mm, "end": v(2.74, -52.75) * mm});
            skLineSegment(sketch, "E27.2.1.4", {"start": v(2.74, -67.25) * mm, "end": v(-2.74, -67.25) * mm});
            skLineSegment(sketch, "E27.3.0.0", {"start": v(40, -20) * mm, "end": v(32.25, -20) * mm, "construction": true});
            skArc(sketch, "E27.3.0.1", {"start": v(42.74, -27.25) * mm, "mid": v(47.75, -20) * mm, "end": v(42.74, -12.75) * mm});
            skArc(sketch, "E27.3.0.2", {"start": v(37.26, -12.75) * mm, "mid": v(32.25, -20) * mm, "end": v(37.26, -27.25) * mm});
            skLineSegment(sketch, "E27.3.0.3", {"start": v(37.26, -12.75) * mm, "end": v(42.74, -12.75) * mm});
            skLineSegment(sketch, "E27.3.0.4", {"start": v(42.74, -27.25) * mm, "end": v(37.26, -27.25) * mm});
            skLineSegment(sketch, "E27.3.1.0", {"start": v(40, -60) * mm, "end": v(32.25, -60) * mm, "construction": true});
            skArc(sketch, "E27.3.1.1", {"start": v(42.74, -67.25) * mm, "mid": v(47.75, -60) * mm, "end": v(42.74, -52.75) * mm});
            skArc(sketch, "E27.3.1.2", {"start": v(37.26, -52.75) * mm, "mid": v(32.25, -60) * mm, "end": v(37.26, -67.25) * mm});
            skLineSegment(sketch, "E27.3.1.3", {"start": v(37.26, -52.75) * mm, "end": v(42.74, -52.75) * mm});
            skLineSegment(sketch, "E27.3.1.4", {"start": v(42.74, -67.25) * mm, "end": v(37.26, -67.25) * mm});
            skLineSegment(sketch, "E27.4.0.0", {"start": v(80, -20) * mm, "end": v(72.25, -20) * mm, "construction": true});
            skArc(sketch, "E27.4.0.1", {"start": v(82.74, -27.25) * mm, "mid": v(87.75, -20) * mm, "end": v(82.74, -12.75) * mm});
            skArc(sketch, "E27.4.0.2", {"start": v(77.26, -12.75) * mm, "mid": v(72.25, -20) * mm, "end": v(77.26, -27.25) * mm});
            skLineSegment(sketch, "E27.4.0.3", {"start": v(77.26, -12.75) * mm, "end": v(82.74, -12.75) * mm});
            skLineSegment(sketch, "E27.4.0.4", {"start": v(82.74, -27.25) * mm, "end": v(77.26, -27.25) * mm});
            skLineSegment(sketch, "E27.4.1.0", {"start": v(80, -60) * mm, "end": v(72.25, -60) * mm, "construction": true});
            skArc(sketch, "E27.4.1.1", {"start": v(82.74, -67.25) * mm, "mid": v(87.75, -60) * mm, "end": v(82.74, -52.75) * mm});
            skArc(sketch, "E27.4.1.2", {"start": v(77.26, -52.75) * mm, "mid": v(72.25, -60) * mm, "end": v(77.26, -67.25) * mm});
            skLineSegment(sketch, "E27.4.1.3", {"start": v(77.26, -52.75) * mm, "end": v(82.74, -52.75) * mm});
            skLineSegment(sketch, "E27.4.1.4", {"start": v(82.74, -67.25) * mm, "end": v(77.26, -67.25) * mm});
            skLineSegment(sketch, "E27.direction1", {"start": v(-82.74, -27.25) * mm, "end": v(-42.74, -27.25) * mm, "construction": true});
            skLineSegment(sketch, "E27.direction2", {"start": v(-82.74, -27.25) * mm, "end": v(-82.74, -67.25) * mm, "construction": true});
            skLineSegment(sketch, "E28", {"start": v(77.21, 169.95) * mm, "end": v(83.31, 168.87) * mm});
            skLineSegment(sketch, "E29", {"start": v(84.55, 167.4) * mm, "end": v(84.55, 132.6) * mm});
            skLineSegment(sketch, "E30", {"start": v(83.31, 131.13) * mm, "end": v(77.21, 130.05) * mm});
            skLineSegment(sketch, "E31", {"start": v(75.45, 131.53) * mm, "end": v(75.45, 168.47) * mm});
            skLineSegment(sketch, "E32", {"start": v(80, 169.46) * mm, "end": v(80, 130.54) * mm, "construction": true});
            skPoint(sketch, "E33.visualSharp", {"position": v(75.45, 170.26) * mm});
            skArc(sketch, "E33.filletArc", {"start": v(77.21, 169.95) * mm, "mid": v(75.99, 169.62) * mm, "end": v(75.45, 168.47) * mm});
            skPoint(sketch, "E34.visualSharp", {"position": v(84.55, 168.66) * mm});
            skArc(sketch, "E34.filletArc", {"start": v(84.55, 167.4) * mm, "mid": v(84.2, 168.36) * mm, "end": v(83.31, 168.87) * mm});
            skPoint(sketch, "E35.visualSharp", {"position": v(84.55, 131.34) * mm});
            skArc(sketch, "E35.filletArc", {"start": v(83.31, 131.13) * mm, "mid": v(84.2, 131.64) * mm, "end": v(84.55, 132.6) * mm});
            skPoint(sketch, "E36.visualSharp", {"position": v(75.45, 129.74) * mm});
            skArc(sketch, "E36.filletArc", {"start": v(75.45, 131.53) * mm, "mid": v(75.99, 130.38) * mm, "end": v(77.21, 130.05) * mm});
            skCircle(sketch, "E37", {"center": v(80, 173.52) * mm, "radius": 1 * mm});
            skCircle(sketch, "E38", {"center": v(80, 126.48) * mm, "radius": 1 * mm});
            skLineSegment(sketch, "E39", {"start": v(75.98, 150) * mm, "end": v(76.95, 150) * mm, "construction": true});
            skSolve(sketch);
        }
        {
            var Q0;
            Q0 = qSketchRegion(id + "F0", true);
            extrude(context, id + "F1", {"entities" : qUnion([Q0]), "depth" : 4 * mm});
        }
        {
            var Q0;
            Q0=makeQuery(id+"F1.opExtrude","CAP_FACE",FACE,{"disambiguationData":[OSD([sQuery(id+"F0.wireOp",EDGE,"E0.bottom"),sQuery(id+"F0.wireOp",EDGE,"E0.top"),sQuery(id+"F0.wireOp",EDGE,"E0.left"),sQuery(id+"F0.wireOp",EDGE,"E0.right"),sQuery(id+"F0.wireOp",EDGE,"E1"),sQuery(id+"F0.wireOp",EDGE,"E2"),sQuery(id+"F0.wireOp",EDGE,"E3"),sQuery(id+"F0.wireOp",EDGE,"E5.trimOffspring"),sQuery(id+"F0.wireOp",EDGE,"E6.0.1.0"),sQuery(id+"F0.wireOp",EDGE,"E6.0.1.1"),sQuery(id+"F0.wireOp",EDGE,"E6.0.1.2"),sQuery(id+"F0.wireOp",EDGE,"E6.0.1.4"),sQuery(id+"F0.wireOp",EDGE,"E7.0.1.0"),sQuery(id+"F0.wireOp",EDGE,"E7.3.1.0"),sQuery(id+"F0.wireOp",EDGE,"E7.6.1.0"),sQuery(id+"F0.wireOp",EDGE,"E7.13.1.0"),sQuery(id+"F0.wireOp",EDGE,"E7.0.1.1"),sQuery(id+"F0.wireOp",EDGE,"E7.3.1.1"),sQuery(id+"F0.wireOp",EDGE,"E7.6.1.1"),sQuery(id+"F0.wireOp",EDGE,"E7.13.1.1"),sQuery(id+"F0.wireOp",EDGE,"E7.0.2.0"),sQuery(id+"F0.wireOp",EDGE,"E7.3.2.0"),sQuery(id+"F0.wireOp",EDGE,"E7.6.2.0"),sQuery(id+"F0.wireOp",EDGE,"E7.13.2.0"),sQuery(id+"F0.wireOp",EDGE,"E7.0.2.1"),sQuery(id+"F0.wireOp",EDGE,"E7.3.2.1"),sQuery(id+"F0.wireOp",EDGE,"E7.6.2.1"),sQuery(id+"F0.wireOp",EDGE,"E7.13.2.1"),sQuery(id+"F0.wireOp",EDGE,"E7.0.3.0"),sQuery(id+"F0.wireOp",EDGE,"E7.3.3.0"),sQuery(id+"F0.wireOp",EDGE,"E7.6.3.0"),sQuery(id+"F0.wireOp",EDGE,"E7.13.3.0"),sQuery(id+"F0.wireOp",EDGE,"E7.0.3.1"),sQuery(id+"F0.wireOp",EDGE,"E7.3.3.1"),sQuery(id+"F0.wireOp",EDGE,"E7.6.3.1"),sQuery(id+"F0.wireOp",EDGE,"E7.13.3.1"),sQuery(id+"F0.wireOp",EDGE,"E7.0.4.0"),sQuery(id+"F0.wireOp",EDGE,"E7.3.4.0"),sQuery(id+"F0.wireOp",EDGE,"E7.6.4.0"),sQuery(id+"F0.wireOp",EDGE,"E7.13.4.0"),sQuery(id+"F0.wireOp",EDGE,"E7.0.4.1"),sQuery(id+"F0.wireOp",EDGE,"E7.3.4.1"),sQuery(id+"F0.wireOp",EDGE,"E7.6.4.1"),sQuery(id+"F0.wireOp",EDGE,"E7.13.4.1"),sQuery(id+"F0.wireOp",EDGE,"E9"),sQuery(id+"F0.wireOp",EDGE,"E10"),sQuery(id+"F0.wireOp",EDGE,"E11"),sQuery(id+"F0.wireOp",EDGE,"E13.trimOffspring"),sQuery(id+"F0.wireOp",EDGE,"E14"),sQuery(id+"F0.wireOp",EDGE,"E15"),sQuery(id+"F0.wireOp",EDGE,"E16"),sQuery(id+"F0.wireOp",EDGE,"E17"),sQuery(id+"F0.wireOp",EDGE,"E19.filletArc"),sQuery(id+"F0.wireOp",EDGE,"E20.filletArc"),sQuery(id+"F0.wireOp",EDGE,"E21.filletArc"),sQuery(id+"F0.wireOp",EDGE,"E22.filletArc"),sQuery(id+"F0.wireOp",EDGE,"E23"),sQuery(id+"F0.wireOp",EDGE,"E24"),sQuery(id+"F0.wireOp",EDGE,"E26.0.1.6"),sQuery(id+"F0.wireOp",EDGE,"E26.0.1.7"),sQuery(id+"F0.wireOp",EDGE,"E26.0.1.8"),sQuery(id+"F0.wireOp",EDGE,"E26.0.1.9"),sQuery(id+"F0.wireOp",EDGE,"E26.0.1.10"),sQuery(id+"F0.wireOp",EDGE,"E26.0.1.11"),sQuery(id+"F0.wireOp",EDGE,"E26.0.1.12"),sQuery(id+"F0.wireOp",EDGE,"E26.0.1.13"),sQuery(id+"F0.wireOp",EDGE,"E26.0.1.14"),sQuery(id+"F0.wireOp",EDGE,"E26.0.1.15"),sQuery(id+"F0.wireOp",EDGE,"E26.1.0.6"),sQuery(id+"F0.wireOp",EDGE,"E26.1.0.7"),sQuery(id+"F0.wireOp",EDGE,"E26.1.0.8"),sQuery(id+"F0.wireOp",EDGE,"E26.1.0.9"),sQuery(id+"F0.wireOp",EDGE,"E26.1.0.10"),sQuery(id+"F0.wireOp",EDGE,"E26.1.0.11"),sQuery(id+"F0.wireOp",EDGE,"E26.1.0.12"),sQuery(id+"F0.wireOp",EDGE,"E26.1.0.13"),sQuery(id+"F0.wireOp",EDGE,"E26.1.0.14"),sQuery(id+"F0.wireOp",EDGE,"E26.1.0.15"),sQuery(id+"F0.wireOp",EDGE,"E26.1.1.6"),sQuery(id+"F0.wireOp",EDGE,"E26.1.1.7"),sQuery(id+"F0.wireOp",EDGE,"E26.1.1.8"),sQuery(id+"F0.wireOp",EDGE,"E26.1.1.9"),sQuery(id+"F0.wireOp",EDGE,"E26.1.1.10"),sQuery(id+"F0.wireOp",EDGE,"E26.1.1.11"),sQuery(id+"F0.wireOp",EDGE,"E26.1.1.12"),sQuery(id+"F0.wireOp",EDGE,"E26.1.1.13"),sQuery(id+"F0.wireOp",EDGE,"E26.1.1.14"),sQuery(id+"F0.wireOp",EDGE,"E26.1.1.15"),sQuery(id+"F0.wireOp",EDGE,"E26.2.0.6"),sQuery(id+"F0.wireOp",EDGE,"E26.2.0.7"),sQuery(id+"F0.wireOp",EDGE,"E26.2.0.8"),sQuery(id+"F0.wireOp",EDGE,"E26.2.0.9"),sQuery(id+"F0.wireOp",EDGE,"E26.2.0.10"),sQuery(id+"F0.wireOp",EDGE,"E26.2.0.11"),sQuery(id+"F0.wireOp",EDGE,"E26.2.0.12"),sQuery(id+"F0.wireOp",EDGE,"E26.2.0.13"),sQuery(id+"F0.wireOp",EDGE,"E26.2.0.14"),sQuery(id+"F0.wireOp",EDGE,"E26.2.0.15"),sQuery(id+"F0.wireOp",EDGE,"E26.2.1.6"),sQuery(id+"F0.wireOp",EDGE,"E26.2.1.7"),sQuery(id+"F0.wireOp",EDGE,"E26.2.1.8"),sQuery(id+"F0.wireOp",EDGE,"E26.2.1.9"),sQuery(id+"F0.wireOp",EDGE,"E26.2.1.10"),sQuery(id+"F0.wireOp",EDGE,"E26.2.1.11"),sQuery(id+"F0.wireOp",EDGE,"E26.2.1.12"),sQuery(id+"F0.wireOp",EDGE,"E26.2.1.13"),sQuery(id+"F0.wireOp",EDGE,"E26.2.1.14"),sQuery(id+"F0.wireOp",EDGE,"E26.2.1.15"),sQuery(id+"F0.wireOp",EDGE,"E26.3.0.6"),sQuery(id+"F0.wireOp",EDGE,"E26.3.0.7"),sQuery(id+"F0.wireOp",EDGE,"E26.3.0.8"),sQuery(id+"F0.wireOp",EDGE,"E26.3.0.9"),sQuery(id+"F0.wireOp",EDGE,"E26.3.0.10"),sQuery(id+"F0.wireOp",EDGE,"E26.3.0.11"),sQuery(id+"F0.wireOp",EDGE,"E26.3.0.12"),sQuery(id+"F0.wireOp",EDGE,"E26.3.0.13"),sQuery(id+"F0.wireOp",EDGE,"E26.3.0.14"),sQuery(id+"F0.wireOp",EDGE,"E26.3.0.15"),sQuery(id+"F0.wireOp",EDGE,"E26.3.1.6"),sQuery(id+"F0.wireOp",EDGE,"E26.3.1.7"),sQuery(id+"F0.wireOp",EDGE,"E26.3.1.8"),sQuery(id+"F0.wireOp",EDGE,"E26.3.1.9"),sQuery(id+"F0.wireOp",EDGE,"E26.3.1.10"),sQuery(id+"F0.wireOp",EDGE,"E26.3.1.11"),sQuery(id+"F0.wireOp",EDGE,"E26.3.1.12"),sQuery(id+"F0.wireOp",EDGE,"E26.3.1.13"),sQuery(id+"F0.wireOp",EDGE,"E26.3.1.14"),sQuery(id+"F0.wireOp",EDGE,"E26.3.1.15"),sQuery(id+"F0.wireOp",EDGE,"E26.4.0.6"),sQuery(id+"F0.wireOp",EDGE,"E26.4.0.7"),sQuery(id+"F0.wireOp",EDGE,"E26.4.0.8"),sQuery(id+"F0.wireOp",EDGE,"E26.4.0.9"),sQuery(id+"F0.wireOp",EDGE,"E26.4.0.10"),sQuery(id+"F0.wireOp",EDGE,"E26.4.0.11"),sQuery(id+"F0.wireOp",EDGE,"E26.4.0.12"),sQuery(id+"F0.wireOp",EDGE,"E26.4.0.13"),sQuery(id+"F0.wireOp",EDGE,"E26.4.0.14"),sQuery(id+"F0.wireOp",EDGE,"E26.4.0.15"),sQuery(id+"F0.wireOp",EDGE,"E26.4.1.6"),sQuery(id+"F0.wireOp",EDGE,"E26.4.1.7"),sQuery(id+"F0.wireOp",EDGE,"E26.4.1.8"),sQuery(id+"F0.wireOp",EDGE,"E26.4.1.9"),sQuery(id+"F0.wireOp",EDGE,"E26.4.1.10"),sQuery(id+"F0.wireOp",EDGE,"E26.4.1.11"),sQuery(id+"F0.wireOp",EDGE,"E26.4.1.12"),sQuery(id+"F0.wireOp",EDGE,"E26.4.1.13"),sQuery(id+"F0.wireOp",EDGE,"E26.4.1.14"),sQuery(id+"F0.wireOp",EDGE,"E26.4.1.15"),sQuery(id+"F0.wireOp",EDGE,"E27.0.1.1"),sQuery(id+"F0.wireOp",EDGE,"E27.0.1.2"),sQuery(id+"F0.wireOp",EDGE,"E27.0.1.3"),sQuery(id+"F0.wireOp",EDGE,"E27.0.1.4"),sQuery(id+"F0.wireOp",EDGE,"E27.1.0.1"),sQuery(id+"F0.wireOp",EDGE,"E27.1.0.2"),sQuery(id+"F0.wireOp",EDGE,"E27.1.0.3"),sQuery(id+"F0.wireOp",EDGE,"E27.1.0.4"),sQuery(id+"F0.wireOp",EDGE,"E27.1.1.1"),sQuery(id+"F0.wireOp",EDGE,"E27.1.1.2"),sQuery(id+"F0.wireOp",EDGE,"E27.1.1.3"),sQuery(id+"F0.wireOp",EDGE,"E27.1.1.4"),sQuery(id+"F0.wireOp",EDGE,"E27.2.0.1"),sQuery(id+"F0.wireOp",EDGE,"E27.2.0.2"),sQuery(id+"F0.wireOp",EDGE,"E27.2.0.3"),sQuery(id+"F0.wireOp",EDGE,"E27.2.0.4"),sQuery(id+"F0.wireOp",EDGE,"E27.2.1.1"),sQuery(id+"F0.wireOp",EDGE,"E27.2.1.2"),sQuery(id+"F0.wireOp",EDGE,"E27.2.1.3"),sQuery(id+"F0.wireOp",EDGE,"E27.2.1.4"),sQuery(id+"F0.wireOp",EDGE,"E27.3.0.1"),sQuery(id+"F0.wireOp",EDGE,"E27.3.0.2"),sQuery(id+"F0.wireOp",EDGE,"E27.3.0.3"),sQuery(id+"F0.wireOp",EDGE,"E27.3.0.4"),sQuery(id+"F0.wireOp",EDGE,"E27.3.1.1"),sQuery(id+"F0.wireOp",EDGE,"E27.3.1.2"),sQuery(id+"F0.wireOp",EDGE,"E27.3.1.3"),sQuery(id+"F0.wireOp",EDGE,"E27.3.1.4"),sQuery(id+"F0.wireOp",EDGE,"E27.4.0.1"),sQuery(id+"F0.wireOp",EDGE,"E27.4.0.2"),sQuery(id+"F0.wireOp",EDGE,"E27.4.0.3"),sQuery(id+"F0.wireOp",EDGE,"E27.4.0.4"),sQuery(id+"F0.wireOp",EDGE,"E27.4.1.1"),sQuery(id+"F0.wireOp",EDGE,"E27.4.1.2"),sQuery(id+"F0.wireOp",EDGE,"E27.4.1.3"),sQuery(id+"F0.wireOp",EDGE,"E27.4.1.4")])],"isStart":false});
            var sketch = newSketch(context, id + "F2", { "sketchPlane" : qUnion([Q0])});
            skLineSegment(sketch, "E40.0", {"start": v(-105, 185) * mm, "end": v(105, 185) * mm});
            skLineSegment(sketch, "E41.0", {"start": v(105, 185) * mm, "end": v(105, -185) * mm});
            skLineSegment(sketch, "E42.0", {"start": v(-105, 185) * mm, "end": v(-105, -185) * mm});
            skLineSegment(sketch, "E43.0", {"start": v(-105, -185) * mm, "end": v(105, -185) * mm});
            skLineSegment(sketch, "E44.0", {"start": v(-120, 200) * mm, "end": v(120, 200) * mm});
            skLineSegment(sketch, "E45.0", {"start": v(-120, -200) * mm, "end": v(-120, 200) * mm});
            skLineSegment(sketch, "E46.0", {"start": v(120, -200) * mm, "end": v(120, 200) * mm});
            skLineSegment(sketch, "E47.0", {"start": v(-120, -200) * mm, "end": v(120, -200) * mm});
            skSolve(sketch);
        }
        {
            var Q0;
            Q0=makeQuery(id+"F2.imprint","IMPRINT",FACE,{"disambiguationData":[TD([[makeQuery(id+"F2.imprint","IMPRINT",EDGE,{"derivedFrom":sQuery(id+"F2.wireOp",EDGE,"E40.0")}),1.0]])]});
            extrude(context, id + "F3", {"entities" : qUnion([Q0]), "operationType" : NewBodyOperationType.REMOVE, "oppositeDirection" : true, "depth" : 1.5 * mm});
        }
        {
            var Q0;
            Q0=qCreatedBy(makeId("Top.planeOp"),FACE);
            var sketch = newSketch(context, id + "F4", { "sketchPlane" : qUnion([Q0])});
            skLineSegment(sketch, "E48.bottom", {"start": v(-120, 310) * mm, "end": v(85, 310) * mm});
            skLineSegment(sketch, "E48.top", {"start": v(-120, 210) * mm, "end": v(85, 210) * mm});
            skLineSegment(sketch, "E48.left", {"start": v(-120, 310) * mm, "end": v(-120, 210) * mm});
            skLineSegment(sketch, "E48.right", {"start": v(85, 310) * mm, "end": v(85, 210) * mm});
            skLineSegment(sketch, "E49", {"start": v(-84.93, 267.53) * mm, "end": v(-84.93, 252.47) * mm});
            skLineSegment(sketch, "E50", {"start": v(-82.58, 250.5) * mm, "end": v(-76.73, 251.53) * mm});
            skLineSegment(sketch, "E51", {"start": v(-75.08, 253.5) * mm, "end": v(-75.08, 266.5) * mm});
            skLineSegment(sketch, "E52", {"start": v(-76.73, 268.47) * mm, "end": v(-82.58, 269.5) * mm});
            skLineSegment(sketch, "E53", {"start": v(-80, 269.05) * mm, "end": v(-80, 250.95) * mm, "construction": true});
            skLineSegment(sketch, "E54", {"start": v(-84.92, 260) * mm, "end": v(-75.08, 260) * mm, "construction": true});
            skCircle(sketch, "E55", {"center": v(-80, 272.5) * mm, "radius": 1 * mm});
            skCircle(sketch, "E56", {"center": v(-80, 247.5) * mm, "radius": 1 * mm});
            skPoint(sketch, "E57.visualSharp", {"position": v(-84.92, 269.91) * mm});
            skArc(sketch, "E57.filletArc", {"start": v(-82.58, 269.5) * mm, "mid": v(-84.21, 269.06) * mm, "end": v(-84.92, 267.53) * mm});
            skPoint(sketch, "E58.visualSharp", {"position": v(-84.92, 250.09) * mm});
            skArc(sketch, "E58.filletArc", {"start": v(-84.92, 252.47) * mm, "mid": v(-84.21, 250.94) * mm, "end": v(-82.58, 250.5) * mm});
            skPoint(sketch, "E59.visualSharp", {"position": v(-75.07, 251.82) * mm});
            skArc(sketch, "E59.filletArc", {"start": v(-76.73, 251.53) * mm, "mid": v(-75.54, 252.22) * mm, "end": v(-75.08, 253.5) * mm});
            skPoint(sketch, "E60.visualSharp", {"position": v(-75.07, 268.18) * mm});
            skArc(sketch, "E60.filletArc", {"start": v(-75.08, 266.5) * mm, "mid": v(-75.54, 267.78) * mm, "end": v(-76.73, 268.47) * mm});
            skLineSegment(sketch, "E61.bottom", {"start": v(-45.5, 271.5) * mm, "end": v(-14.5, 271.5) * mm});
            skLineSegment(sketch, "E61.top", {"start": v(-45.5, 248.5) * mm, "end": v(-14.5, 248.5) * mm});
            skLineSegment(sketch, "E61.left", {"start": v(-45.5, 271.5) * mm, "end": v(-45.5, 248.5) * mm});
            skLineSegment(sketch, "E61.right", {"start": v(-14.5, 271.5) * mm, "end": v(-14.5, 248.5) * mm});
            skLineSegment(sketch, "E62", {"start": v(-45.5, 260) * mm, "end": v(-14.5, 260) * mm, "construction": true});
            skCircle(sketch, "E63", {"center": v(-10, 260) * mm, "radius": 1.65 * mm});
            skLineSegment(sketch, "E64", {"start": v(-30, 271.5) * mm, "end": v(-30, 248.5) * mm, "construction": true});
            skCircle(sketch, "E65", {"center": v(-50, 260) * mm, "radius": 1.65 * mm});
            skLineSegment(sketch, "E66.bottom", {"start": v(13.85, 282) * mm, "end": v(56.15, 282) * mm});
            skLineSegment(sketch, "E66.top", {"start": v(13.85, 238) * mm, "end": v(56.15, 238) * mm});
            skLineSegment(sketch, "E66.left", {"start": v(13.85, 282) * mm, "end": v(13.85, 238) * mm});
            skLineSegment(sketch, "E66.right", {"start": v(56.15, 282) * mm, "end": v(56.15, 238) * mm});
            skLineSegment(sketch, "E67.bottom", {"start": v(13.85, 260) * mm, "end": v(56.15, 260) * mm, "construction": true});
            skLineSegment(sketch, "E67.top", {"start": v(13.85, 260) * mm, "end": v(56.15, 260) * mm, "construction": true});
            skLineSegment(sketch, "E67.left", {"start": v(13.85, 260) * mm, "end": v(13.85, 260) * mm});
            skLineSegment(sketch, "E67.right", {"start": v(56.15, 260) * mm, "end": v(56.15, 260) * mm});
            skLineSegment(sketch, "E68", {"start": v(35, 282) * mm, "end": v(35, 238) * mm, "construction": true});
            skSolve(sketch);
        }
        {
            var Q0;
            Q0 = qSketchRegion(id + "F4", true);
            extrude(context, id + "F5", {"entities" : qUnion([Q0]), "depth" : 4 * mm});
        }
        {
            var Q0;
            Q0=makeQuery(id+"F5.opExtrude","CAP_FACE",FACE,{"disambiguationData":[OSD([sQuery(id+"F4.wireOp",EDGE,"E48.bottom"),sQuery(id+"F4.wireOp",EDGE,"E48.top"),sQuery(id+"F4.wireOp",EDGE,"E48.left"),sQuery(id+"F4.wireOp",EDGE,"E48.right"),sQuery(id+"F4.wireOp",EDGE,"E49"),sQuery(id+"F4.wireOp",EDGE,"E50"),sQuery(id+"F4.wireOp",EDGE,"E51"),sQuery(id+"F4.wireOp",EDGE,"E52"),sQuery(id+"F4.wireOp",EDGE,"E55"),sQuery(id+"F4.wireOp",EDGE,"E56"),sQuery(id+"F4.wireOp",EDGE,"E57.filletArc"),sQuery(id+"F4.wireOp",EDGE,"E58.filletArc"),sQuery(id+"F4.wireOp",EDGE,"E59.filletArc"),sQuery(id+"F4.wireOp",EDGE,"E60.filletArc"),sQuery(id+"F4.wireOp",EDGE,"E61.bottom"),sQuery(id+"F4.wireOp",EDGE,"E61.top"),sQuery(id+"F4.wireOp",EDGE,"E61.left"),sQuery(id+"F4.wireOp",EDGE,"E61.right"),sQuery(id+"F4.wireOp",EDGE,"E63"),sQuery(id+"F4.wireOp",EDGE,"E65"),sQuery(id+"F4.wireOp",EDGE,"E66.bottom"),sQuery(id+"F4.wireOp",EDGE,"E66.top"),sQuery(id+"F4.wireOp",EDGE,"E66.left"),sQuery(id+"F4.wireOp",EDGE,"E66.right")])],"isStart":false});
            var sketch = newSketch(context, id + "F6", { "sketchPlane" : qUnion([Q0])});
            skLineSegment(sketch, "E69.bottom", {"start": v(-105, 295) * mm, "end": v(70, 295) * mm});
            skLineSegment(sketch, "E69.top", {"start": v(-105, 225) * mm, "end": v(70, 225) * mm});
            skLineSegment(sketch, "E69.left", {"start": v(-105, 295) * mm, "end": v(-105, 225) * mm});
            skLineSegment(sketch, "E69.right", {"start": v(70, 295) * mm, "end": v(70, 225) * mm});
            skLineSegment(sketch, "E70.0", {"start": v(-120, 310) * mm, "end": v(85, 310) * mm});
            skLineSegment(sketch, "E71.0", {"start": v(-120, 310) * mm, "end": v(-120, 210) * mm});
            skLineSegment(sketch, "E72.0", {"start": v(-120, 210) * mm, "end": v(85, 210) * mm});
            skLineSegment(sketch, "E73.0", {"start": v(85, 310) * mm, "end": v(85, 210) * mm});
            skSolve(sketch);
        }
        {
            var Q0;
            Q0 = qSketchRegion(id + "F6", true);
            extrude(context, id + "F7", {"entities" : qUnion([Q0]), "operationType" : NewBodyOperationType.REMOVE, "oppositeDirection" : true, "depth" : 1.5 * mm});
        }
    });
